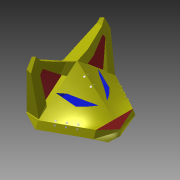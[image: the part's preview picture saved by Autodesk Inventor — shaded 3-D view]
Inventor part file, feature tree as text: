
AUTODESK INVENTOR PART (.ipt)
format: ipt  version: 2014 (Build 180170000, 170)  size: 505,856 bytes
history: native  units: in
note: dims shown in document units (in); Inventor stores cm internally (conversion verified against a paired STEP export)
features: sketch x14, extrude x8, plane x7, loft x4, projected_geometry x4, other x3, mirror x1
ambient origin geometry x8: Origin, YZ Plane, XZ Plane, XY Plane, X Axis, Y Axis, Z Axis, Center Point
bodies: Solid1 (feature_tree)
feature tree (41):
  sketch  "Sketch1"  dims[d0=0.7559in d1=0.7559in]
  plane  "Work Plane1"
  loft  "Loft1"
  extrude  "Extrusion1"  Depth=0.2in
  plane  "Work Plane4"
  loft  "Loft2"
  plane  "Work Plane5"
  loft  "Loft3"
  loft  "Loft4"
  extrude  "Extrusion2"  TaperAngle=0.0deg  [1 undecoded]
  plane  "Work Plane6"
  extrude  "Extrusion3"  Depth=1.0in
  extrude  "Extrusion4"  Depth=1.0651in
  extrude  "Extrusion5"  Depth=0.962in
  plane  "Work Plane7"
  extrude  "Extrusion6"  Depth=0.075in
  plane  "Work Plane8"
  other  "Work Axis1"
  plane  "Work Plane9"
  extrude  "Extrusion7"  Depth=0.06in
  mirror  "Mirror3"
  extrude  "Extrusion8"  Depth=0.05in
  sketch  "Sketch2"  dims[d2=0.9963in d3=0.2in]
  sketch  "Sketch3"  dims[d4=0.5in d6=0.08in]
  sketch  "Sketch4"  dims[d7=0.45in d8=150.0deg]
  other  "Edges1"
  sketch  "Sketch5"  dims[d9=150.0deg d14=0.33in]
  projected_geometry  "Projected Loop1"
  other  "Edges2"
  sketch  "Sketch6"  dims[d15=0.66in d18=0.0in d19=90.0deg]
  sketch  "Sketch7"  dims[d20=0.0in d21=90.0deg d22=1.0in]
  sketch  "Sketch8"  dims[d26=1.0651in d28=1.0651in]
  sketch  "Sketch9"  dims[d29=0.0in d30=0.962in]
  sketch  "Sketch10"  dims[d31=0.962in d32=0.075in]
  sketch  "Sketch11"  dims[d33=0.15in d34=0.06in]
  sketch  "Sketch12"  dims[d35=0.1in d36=0.05in]
  sketch  "Sketch13"  dims[d37=0.45in d38=0.0in]
  projected_geometry  "Projected Loop2"
  projected_geometry  "Projected Loop3"
  sketch  "Sketch14"  dims[d39=0.0625in d40=0.01in d41=0.075in d42=0.01in d43=0.0in d44=90.0deg d45=0.0in d46=90.0deg d47=0.2in d48=0.07in d49=0.0in d50=90.0deg d51=0.0in d52=90.0deg d53=0.01in d54=0.01in d55=0.0344in d56=150.0deg d57=60.0deg d58=150.0deg d59=0.7in d60=0.05in d61=0.05in d62=0.05in d63=0.05in d64=0.05in d65=0.01in d66=0.0in d67=90.0deg d68=0.0in d69=90.0deg d70=0.1in d71=0.4in d72=0.15in d73=0.05in d74=0.0in d75=0.02in d77=0.15in d78=0.02in d79=0.1in d80=0.1in d81=0.1in d82=0.02in d83=0.15in d84=0.05in d85=0.0in d86=0.045in d87=0.0in d88=0.025in d89=0.0in d90=0.02in d91=0.02in d92=0.005in d93=0.0in d94=90.0deg d95=0.4466in d96=1.0in d97=0.0in d98=1.0in d99=0.0in d100=0.6528in]
  projected_geometry  "Projected Loop4"
note: 1 required parameter value undecoded (feature->parameter linkage not recoverable at this tier; creation-order binding heuristic only, values carry confidence <= 0.55)
